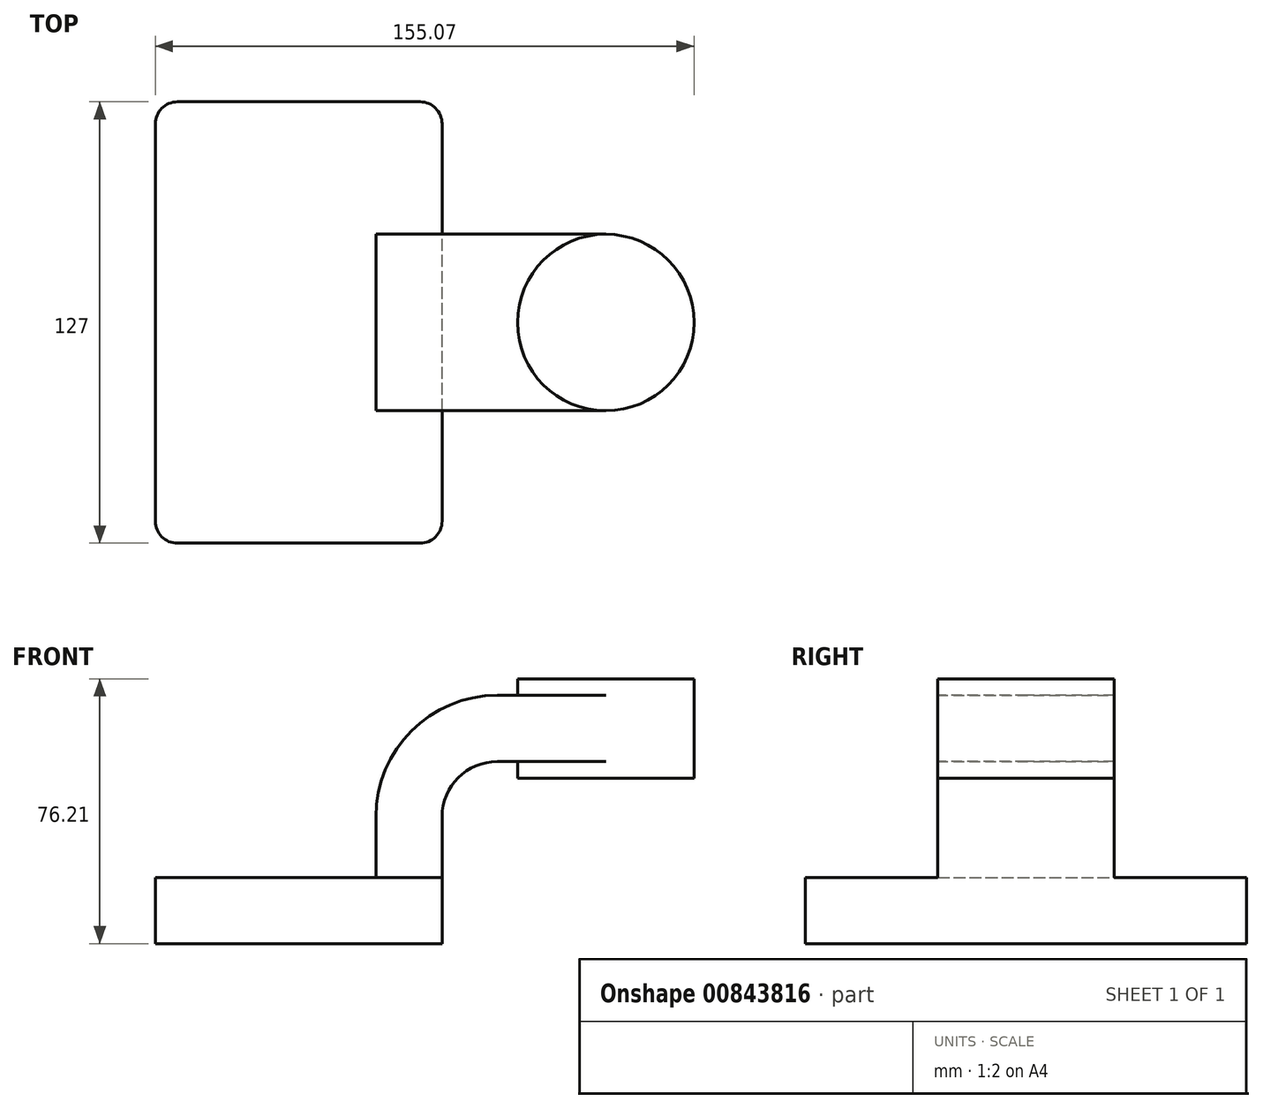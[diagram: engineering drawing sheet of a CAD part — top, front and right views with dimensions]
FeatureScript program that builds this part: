
annotation { "Feature Type Name" : "Feature", "Feature Type Description" : "" }
export const myFeature = defineFeature(function(context is Context, id is Id, definition is map)
    precondition{}
    {
        {
            var Q0;
            Q0=qCreatedBy(makeId("Front.planeOp"),FACE);
            var sketch = newSketch(context, id + "F0", { "sketchPlane" : qUnion([Q0])});
            skLineSegment(sketch, "E0.bottom", {"start": v(41.27, 9.53) * mm, "end": v(-41.28, 9.53) * mm});
            skLineSegment(sketch, "E0.top", {"start": v(41.28, -9.52) * mm, "end": v(-41.27, -9.52) * mm});
            skLineSegment(sketch, "E0.left", {"start": v(41.28, 9.53) * mm, "end": v(41.28, -9.52) * mm});
            skLineSegment(sketch, "E0.right", {"start": v(-41.28, 9.53) * mm, "end": v(-41.27, -9.52) * mm});
            skPoint(sketch, "E0.middle", {"position": v(0, 0) * mm});
            skLineSegment(sketch, "E1.bottom", {"start": v(113.8, 38.1) * mm, "end": v(63, 38.1) * mm});
            skLineSegment(sketch, "E1.top", {"start": v(113.8, 66.68) * mm, "end": v(63, 66.68) * mm});
            skLineSegment(sketch, "E1.left", {"start": v(113.8, 38.1) * mm, "end": v(113.8, 66.68) * mm});
            skLineSegment(sketch, "E1.right", {"start": v(63, 38.1) * mm, "end": v(63, 66.68) * mm});
            skPoint(sketch, "E1.middle", {"position": v(88.4, 52.39) * mm});
            skLineSegment(sketch, "E2", {"start": v(41.27, 9.53) * mm, "end": v(41.27, 26.99) * mm});
            skArc(sketch, "E3", {"start": v(41.27, 26.99) * mm, "mid": v(45.92, 38.21) * mm, "end": v(57.15, 42.86) * mm});
            skLineSegment(sketch, "E4", {"start": v(57.15, 42.86) * mm, "end": v(88.4, 42.86) * mm});
            skLineSegment(sketch, "E5.0", {"start": v(57.15, 61.91) * mm, "end": v(88.4, 61.91) * mm});
            skArc(sketch, "E5.1", {"start": v(22.22, 26.99) * mm, "mid": v(32.45, 51.68) * mm, "end": v(57.15, 61.91) * mm});
            skLineSegment(sketch, "E5.2", {"start": v(22.22, 9.53) * mm, "end": v(22.22, 26.99) * mm});
            skLineSegment(sketch, "E6", {"start": v(88.4, 38.1) * mm, "end": v(88.4, 66.68) * mm});
            skFitSpline(sketch, "E7", {"points": [v(-41.28, 9.53) * mm, v(57.15, 61.91) * mm], "startDerivative": vector(60.82, 116.83) * mm, "endDerivative": vector(100.13, -3.98) * mm});
            skSolve(sketch);
        }
        {
            var Q0;
            Q0=makeQuery(id+"F0.imprint","IMPRINT",FACE,{"disambiguationData":[TD([[makeQuery(id+"F0.imprint","IMPRINT",EDGE,{"derivedFrom":sQuery(id+"F0.wireOp",EDGE,"E0.top")}),-1.0]])]});
            extrude(context, id + "F1", {"entities" : qUnion([Q0]), "endBound" : BoundingType.SYMMETRIC, "depth" : 127 * mm, "offsetDistance" : 25.4 * mm});
        }
        {
            var Q0;
            {var subQ1=sQuery(id+"F0.wireOp",EDGE,"E2");Q0=makeQuery(id+"F0.imprint","IMPRINT",FACE,{"disambiguationData":[TD([[makeQuery(id+"F0.imprint","IMPRINT",EDGE,{"derivedFrom":subQ1}),1.0]])]});}
            var Q1;
            {var subQ0=sQuery(id+"F0.wireOp",EDGE,"E4");var subQ1=sQuery(id+"F0.wireOp",EDGE,"E1.right");var subQ2=makeQuery(id+"F0.imprint","INTERSECT",VERTEX,{"derivedFrom":[subQ1,subQ0]});Q1=makeQuery(id+"F0.imprint","IMPRINT",FACE,{"disambiguationData":[TD([[makeQuery(id+"F0.imprint","IMPRINT",EDGE,{"disambiguationData":[TD([[subQ2,-1.0]])],"derivedFrom":subQ1}),-1.0]])]});}
            extrude(context, id + "F2", {"entities" : qUnion([Q0, Q1]), "operationType" : NewBodyOperationType.ADD, "endBound" : BoundingType.SYMMETRIC, "depth" : 50.8 * mm, "offsetDistance" : 25.4 * mm});
        }
        {
            var Q0;
            Q0=makeQuery(id+"F0.imprint","IMPRINT",FACE,{"disambiguationData":[TD([[makeQuery(id+"F0.imprint","IMPRINT",EDGE,{"derivedFrom":sQuery(id+"F0.wireOp",EDGE,"E5.1")}),1.0]])]});
            extrude(context, id + "F3", {"entities" : qUnion([Q0]), "operationType" : NewBodyOperationType.ADD, "endBound" : BoundingType.SYMMETRIC, "depth" : 15.88 * mm, "offsetDistance" : 25.4 * mm});
        }
        {
            var Q0;
            {var subQ4=sQuery(id+"F0.wireOp",EDGE,"E1.left");Q0=makeQuery(id+"F0.imprint","IMPRINT",FACE,{"disambiguationData":[TD([[makeQuery(id+"F0.imprint","IMPRINT",EDGE,{"derivedFrom":subQ4}),1.0]])]});}
            var Q1;
            Q1=sQuery(id+"F0.wireOp",EDGE,"E6");
            revolve(context, id + "F4", {"operationType" : NewBodyOperationType.ADD, "surfaceOperationType" : NewSurfaceOperationType.NEW, "entities" : qUnion([Q0]), "axis" : qUnion([Q1]), "revolveType" : RevolveType.FULL});
        }
        {
            var Q0;
            Q0=makeQuery(id+"F1.opExtrude","CAP_EDGE",EDGE,{"disambiguationData":[OSD([sQuery(id+"F0.wireOp",EDGE,"E0.left")])],"isStart":false});
            var Q1;
            Q1=makeQuery(id+"F1.opExtrude","CAP_EDGE",EDGE,{"disambiguationData":[OSD([sQuery(id+"F0.wireOp",EDGE,"E0.right")])],"isStart":false});
            var Q2;
            Q2=makeQuery(id+"F1.opExtrude","CAP_EDGE",EDGE,{"disambiguationData":[OSD([sQuery(id+"F0.wireOp",EDGE,"E0.left")])],"isStart":true});
            var Q3;
            Q3=makeQuery(id+"F1.opExtrude","CAP_EDGE",EDGE,{"disambiguationData":[OSD([sQuery(id+"F0.wireOp",EDGE,"E0.right")])],"isStart":true});
            fillet(context, id + "F5", {"entities" : qUnion([Q0, Q1, Q2, Q3]), "radius" : 6.35 * mm, "tangentPropagation" : true, "allowEdgeOverflow" : false});
        }
    });
